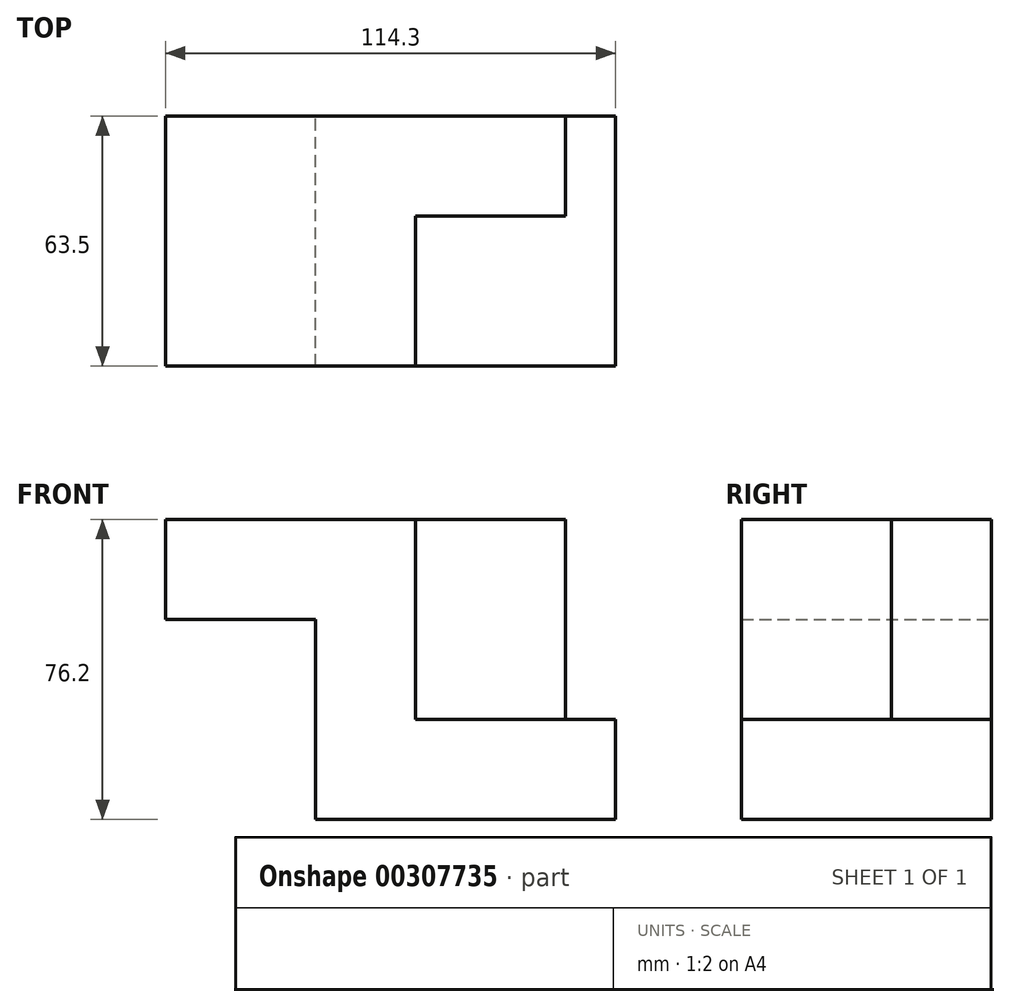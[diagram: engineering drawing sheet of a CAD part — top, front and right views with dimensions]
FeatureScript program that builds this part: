
annotation { "Feature Type Name" : "Feature", "Feature Type Description" : "" }
export const myFeature = defineFeature(function(context is Context, id is Id, definition is map)
    precondition{}
    {
        {
            var Q0;
            Q0=qCreatedBy(makeId("Top.planeOp"),FACE);
            var sketch = newSketch(context, id + "F0", { "sketchPlane" : qUnion([Q0])});
            skLineSegment(sketch, "E0", {"start": v(45.37, 39.81) * mm, "end": v(45.37, -23.69) * mm});
            skLineSegment(sketch, "E1", {"start": v(45.37, -23.69) * mm, "end": v(-30.83, -23.69) * mm});
            skLineSegment(sketch, "E2", {"start": v(-30.83, -23.69) * mm, "end": v(-30.83, 39.81) * mm});
            skLineSegment(sketch, "E3", {"start": v(-30.83, 39.81) * mm, "end": v(45.37, 39.81) * mm});
            skSolve(sketch);
        }
        {
            var Q0;
            Q0 = qSketchRegion(id + "F0", true);
            extrude(context, id + "F1", {"entities" : qUnion([Q0]), "depth" : 25.4 * mm});
        }
        {
            var Q0;
            Q0=makeQuery(id+"F1.opExtrude","CAP_FACE",FACE,{"disambiguationData":[OSD([sQuery(id+"F0.wireOp",EDGE,"E0"),sQuery(id+"F0.wireOp",EDGE,"E1"),sQuery(id+"F0.wireOp",EDGE,"E2"),sQuery(id+"F0.wireOp",EDGE,"E3")])],"isStart":false});
            var sketch = newSketch(context, id + "F2", { "sketchPlane" : qUnion([Q0])});
            skLineSegment(sketch, "E4", {"start": v(-30.83, -23.69) * mm, "end": v(-5.43, -23.69) * mm});
            skLineSegment(sketch, "E5", {"start": v(-5.43, -23.69) * mm, "end": v(-5.43, 14.41) * mm});
            skLineSegment(sketch, "E6", {"start": v(-5.43, 14.41) * mm, "end": v(32.67, 14.41) * mm});
            skLineSegment(sketch, "E7", {"start": v(32.67, 14.41) * mm, "end": v(32.67, 39.81) * mm});
            skLineSegment(sketch, "E8", {"start": v(32.67, 39.81) * mm, "end": v(-30.83, 39.81) * mm});
            skLineSegment(sketch, "E9", {"start": v(-30.83, 39.81) * mm, "end": v(-30.83, -23.69) * mm});
            skSolve(sketch);
        }
        {
            var Q0;
            Q0 = qSketchRegion(id + "F2", true);
            extrude(context, id + "F3", {"entities" : qUnion([Q0]), "operationType" : NewBodyOperationType.ADD, "depth" : 50.8 * mm});
        }
        {
            var Q0;
            Q0=makeQuery(id+"F3.boolean.opBoolean","MERGE",FACE,{"derivedFrom":[makeQuery(id+"F1.opExtrude","SWEPT_FACE",FACE,{"disambiguationData":[OSD([sQuery(id+"F0.wireOp",EDGE,"E2")])]}),makeQuery(id+"F3.opExtrude","SWEPT_FACE",FACE,{"disambiguationData":[OSD([sQuery(id+"F2.wireOp",EDGE,"E9")])]})]});
            var sketch = newSketch(context, id + "F4", { "sketchPlane" : qUnion([Q0])});
            skLineSegment(sketch, "E10", {"start": v(-39.81, 76.2) * mm, "end": v(23.69, 76.2) * mm});
            skLineSegment(sketch, "E11", {"start": v(23.69, 76.2) * mm, "end": v(23.69, 50.8) * mm});
            skLineSegment(sketch, "E12", {"start": v(23.69, 50.8) * mm, "end": v(-39.81, 50.8) * mm});
            skLineSegment(sketch, "E13", {"start": v(-39.81, 50.8) * mm, "end": v(-39.81, 76.2) * mm});
            skSolve(sketch);
        }
        {
            var Q0;
            Q0=makeQuery(id+"F4.imprint","IMPRINT",FACE,{"disambiguationData":[TD([[makeQuery(id+"F4.imprint","IMPRINT",EDGE,{"derivedFrom":sQuery(id+"F4.wireOp",EDGE,"E10")}),1.0]])]});
            extrude(context, id + "F5", {"entities" : qUnion([Q0]), "operationType" : NewBodyOperationType.ADD, "depth" : 38.1 * mm});
        }
    });
